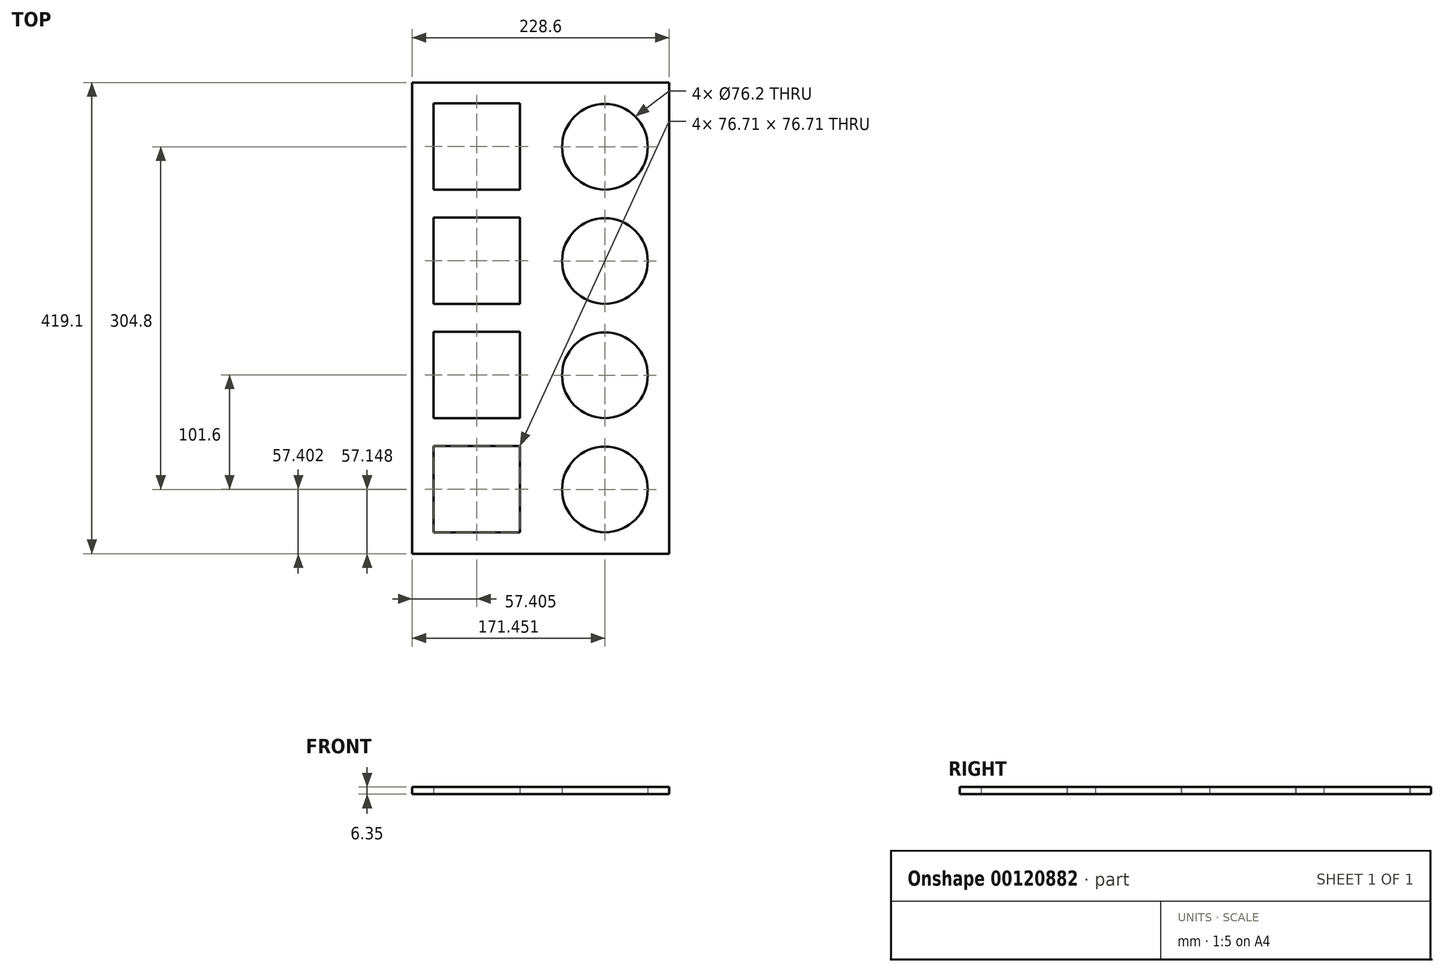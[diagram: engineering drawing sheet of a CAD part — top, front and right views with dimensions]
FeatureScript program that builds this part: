
annotation { "Feature Type Name" : "Feature", "Feature Type Description" : "" }
export const myFeature = defineFeature(function(context is Context, id is Id, definition is map)
    precondition{}
    {
        {
            var Q0;
            Q0=qCreatedBy(makeId("Top.planeOp"),FACE);
            var sketch = newSketch(context, id + "F0", { "sketchPlane" : qUnion([Q0])});
            skLineSegment(sketch, "E0.bottom", {"start": v(-97.95, 225.15) * mm, "end": v(130.65, 225.15) * mm});
            skLineSegment(sketch, "E0.top", {"start": v(-97.95, -193.95) * mm, "end": v(130.65, -193.95) * mm});
            skLineSegment(sketch, "E0.left", {"start": v(-97.95, 225.15) * mm, "end": v(-97.95, -193.95) * mm});
            skLineSegment(sketch, "E0.right", {"start": v(130.65, 225.15) * mm, "end": v(130.65, -193.95) * mm});
            skSolve(sketch);
        }
        {
            var Q0;
            Q0=makeQuery(id+"F0.imprint","IMPRINT",FACE,{"disambiguationData":[TD([[makeQuery(id+"F0.imprint","IMPRINT",EDGE,{"derivedFrom":sQuery(id+"F0.wireOp",EDGE,"E0.bottom")}),-1.0]])]});
            extrude(context, id + "F1", {"entities" : qUnion([Q0]), "depth" : 6.35 * mm});
        }
        {
            var Q0;
            Q0=makeQuery(id+"F1.opExtrude","CAP_FACE",FACE,{"disambiguationData":[OSD([sQuery(id+"F0.wireOp",EDGE,"E0.bottom"),sQuery(id+"F0.wireOp",EDGE,"E0.top"),sQuery(id+"F0.wireOp",EDGE,"E0.left"),sQuery(id+"F0.wireOp",EDGE,"E0.right")])],"isStart":true});
            var sketch = newSketch(context, id + "F2", { "sketchPlane" : qUnion([Q0])});
            skLineSegment(sketch, "E1.bottom", {"start": v(-78.9, 174.9) * mm, "end": v(-2.2, 174.9) * mm});
            skLineSegment(sketch, "E1.top", {"start": v(-78.9, 98.2) * mm, "end": v(-2.2, 98.2) * mm});
            skLineSegment(sketch, "E1.left", {"start": v(-78.9, 174.9) * mm, "end": v(-78.9, 98.2) * mm});
            skLineSegment(sketch, "E1.right", {"start": v(-2.2, 174.9) * mm, "end": v(-2.2, 98.2) * mm});
            skLineSegment(sketch, "E2.0.1.0", {"start": v(-78.9, 73.3) * mm, "end": v(-2.2, 73.3) * mm});
            skLineSegment(sketch, "E2.0.1.1", {"start": v(-78.9, 73.3) * mm, "end": v(-78.9, -3.4) * mm});
            skLineSegment(sketch, "E2.0.1.2", {"start": v(-2.2, 73.3) * mm, "end": v(-2.2, -3.4) * mm});
            skLineSegment(sketch, "E2.0.1.3", {"start": v(-78.9, -3.4) * mm, "end": v(-2.2, -3.4) * mm});
            skLineSegment(sketch, "E2.0.2.0", {"start": v(-78.9, -28.3) * mm, "end": v(-2.2, -28.3) * mm});
            skLineSegment(sketch, "E2.0.2.1", {"start": v(-78.9, -28.3) * mm, "end": v(-78.9, -105) * mm});
            skLineSegment(sketch, "E2.0.2.2", {"start": v(-2.2, -28.3) * mm, "end": v(-2.2, -105) * mm});
            skLineSegment(sketch, "E2.0.2.3", {"start": v(-78.9, -105) * mm, "end": v(-2.2, -105) * mm});
            skLineSegment(sketch, "E2.0.3.0", {"start": v(-78.9, -129.9) * mm, "end": v(-2.2, -129.9) * mm});
            skLineSegment(sketch, "E2.0.3.1", {"start": v(-78.9, -129.9) * mm, "end": v(-78.9, -206.6) * mm});
            skLineSegment(sketch, "E2.0.3.2", {"start": v(-2.2, -129.9) * mm, "end": v(-2.2, -206.6) * mm});
            skLineSegment(sketch, "E2.0.3.3", {"start": v(-78.9, -206.6) * mm, "end": v(-2.2, -206.6) * mm});
            skLineSegment(sketch, "E2.direction1", {"start": v(-78.9, 98.2) * mm, "end": v(-104.3, 98.2) * mm, "construction": true});
            skLineSegment(sketch, "E2.direction2", {"start": v(-78.9, 98.2) * mm, "end": v(-78.9, -3.4) * mm, "construction": true});
            skSolve(sketch);
        }
        {
            var Q0;
            Q0 = qSketchRegion(id + "F2", true);
            extrude(context, id + "F3", {"entities" : qUnion([Q0]), "operationType" : NewBodyOperationType.REMOVE, "oppositeDirection" : true, "depth" : 25.4 * mm});
        }
        {
            var Q0;
            Q0=makeQuery(id+"F1.opExtrude","CAP_FACE",FACE,{"disambiguationData":[OSD([sQuery(id+"F0.wireOp",EDGE,"E0.bottom"),sQuery(id+"F0.wireOp",EDGE,"E0.top"),sQuery(id+"F0.wireOp",EDGE,"E0.left"),sQuery(id+"F0.wireOp",EDGE,"E0.right")])],"isStart":true});
            var sketch = newSketch(context, id + "F4", { "sketchPlane" : qUnion([Q0])});
            skCircle(sketch, "E3", {"center": v(73.5, 136.8) * mm, "radius": 38.1 * mm});
            skCircle(sketch, "E4.0.1.0", {"center": v(73.5, 35.2) * mm, "radius": 38.1 * mm});
            skCircle(sketch, "E4.0.2.0", {"center": v(73.5, -66.4) * mm, "radius": 38.1 * mm});
            skCircle(sketch, "E4.0.3.0", {"center": v(73.5, -168) * mm, "radius": 38.1 * mm});
            skLineSegment(sketch, "E4.direction1", {"start": v(73.5, 136.8) * mm, "end": v(98.9, 136.8) * mm, "construction": true});
            skLineSegment(sketch, "E4.direction2", {"start": v(73.5, 136.8) * mm, "end": v(73.5, 35.2) * mm, "construction": true});
            skSolve(sketch);
        }
        {
            var Q0;
            Q0 = qSketchRegion(id + "F4", true);
            extrude(context, id + "F5", {"entities" : qUnion([Q0]), "operationType" : NewBodyOperationType.REMOVE, "oppositeDirection" : true, "depth" : 25.4 * mm});
        }
    });
